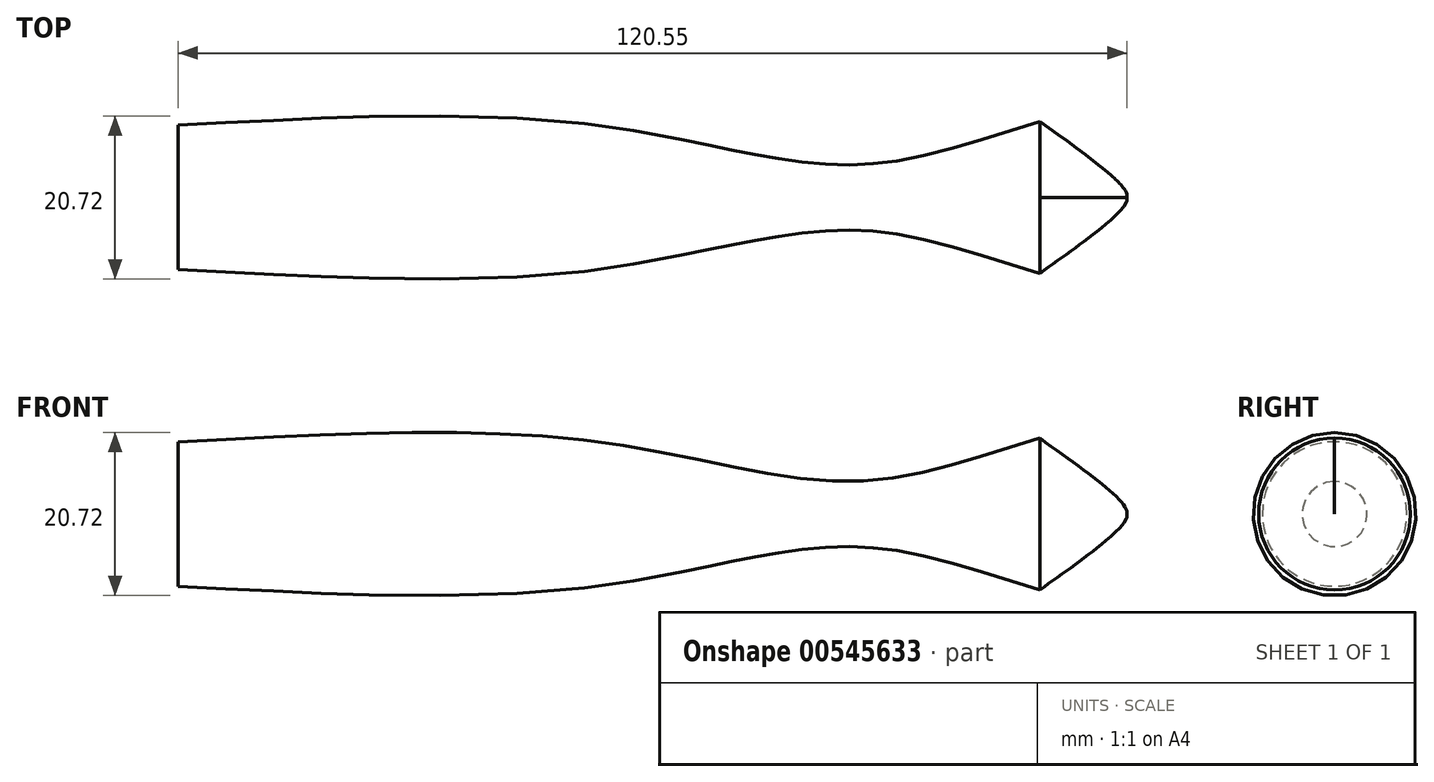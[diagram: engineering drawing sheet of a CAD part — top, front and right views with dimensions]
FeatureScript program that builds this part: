
annotation { "Feature Type Name" : "Feature", "Feature Type Description" : "" }
export const myFeature = defineFeature(function(context is Context, id is Id, definition is map)
    precondition{}
    {
        {
            var Q0;
            Q0=qCreatedBy(makeId("Front.planeOp"),FACE);
            var sketch = newSketch(context, id + "F0", { "sketchPlane" : qUnion([Q0])});
            skLineSegment(sketch, "E0", {"start": v(-53.29, 0) * mm, "end": v(58.32, 0) * mm});
            skPoint(sketch, "E1.0.internal.orphan", {"position": v(-53.29, 0) * mm});
            skPoint(sketch, "E1.5.internal.orphan", {"position": v(58.32, 0) * mm});
            skLineSegment(sketch, "E2", {"start": v(-53.29, 0) * mm, "end": v(-53.29, 9.18) * mm});
            skFitSpline(sketch, "E3", {"points": [v(-53.29, 9.18) * mm, v(0, 9.18) * mm, v(32.57, 4.14) * mm, v(56.17, 9.64) * mm], "startDerivative": vector(140.15, 7.3) * mm, "endDerivative": vector(89.3, 25.92) * mm});
            skFitSpline(sketch, "E4", {"points": [v(56.17, 9.64) * mm, v(67.23, 0) * mm, v(58.32, 0) * mm], "startDerivative": vector(30.93, -21.97) * mm, "endDerivative": vector(-29.1, 3.76) * mm});
            skLineSegment(sketch, "E5", {"start": v(58.32, 0) * mm, "end": v(67.23, 0) * mm});
            skSolve(sketch);
        }
        {
            var Q0;
            Q0=makeQuery(id+"F0.imprint","IMPRINT",FACE,{"disambiguationData":[TD([[makeQuery(id+"F0.imprint","IMPRINT",EDGE,{"derivedFrom":sQuery(id+"F0.wireOp",EDGE,"E0")}),1.0]])]});
            var Q1;
            Q1=sQuery(id+"F0.wireOp",EDGE,"E0");
            revolve(context, id + "F1", {"entities" : qUnion([Q0]), "axis" : qUnion([Q1]), "revolveType" : RevolveType.FULL});
        }
    });
